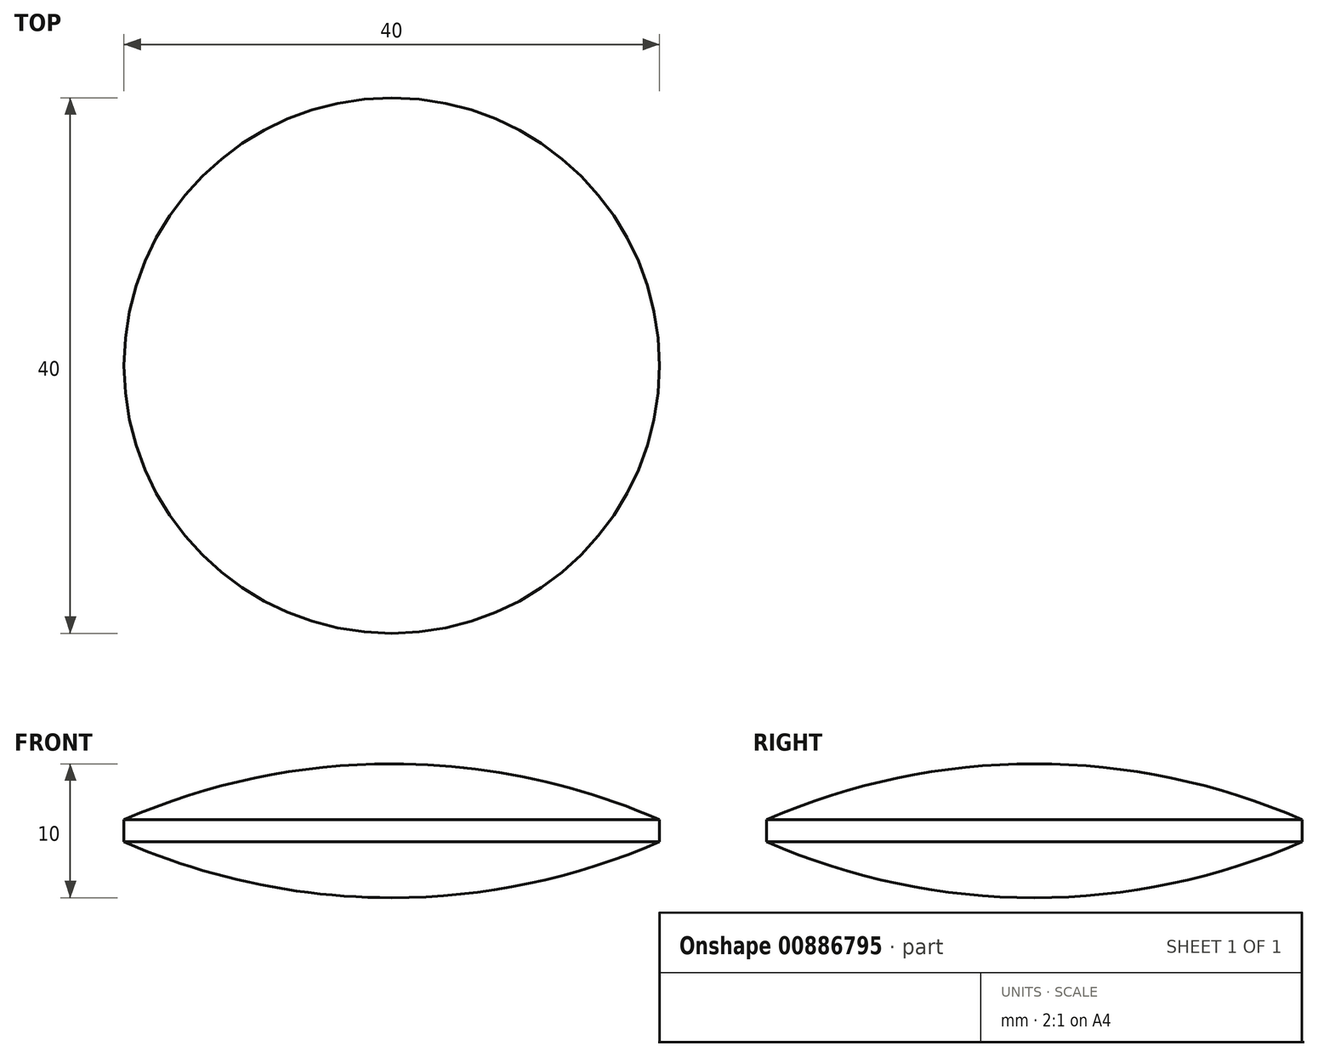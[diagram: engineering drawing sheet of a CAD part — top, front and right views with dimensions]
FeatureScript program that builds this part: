
annotation { "Feature Type Name" : "Feature", "Feature Type Description" : "" }
export const myFeature = defineFeature(function(context is Context, id is Id, definition is map)
    precondition{}
    {
        {
            var Q0;
            Q0=qCreatedBy(makeId("Front.planeOp"),FACE);
            var sketch = newSketch(context, id + "F0", { "sketchPlane" : qUnion([Q0])});
            skArc(sketch, "E0", {"start": v(-20, -0.83) * mm, "mid": v(-10.22, -3.95) * mm, "end": v(0, -5) * mm});
            skArc(sketch, "E1", {"start": v(0, 5) * mm, "mid": v(-10.22, 3.95) * mm, "end": v(-20, 0.83) * mm});
            skLineSegment(sketch, "E2", {"start": v(0, -5) * mm, "end": v(0, 5) * mm});
            skLineSegment(sketch, "E3", {"start": v(-20, -0.83) * mm, "end": v(-20, 0.83) * mm});
            skPoint(sketch, "E4.orphan", {"position": v(-20, -6.59) * mm});
            skSolve(sketch);
        }
        {
            var Q0;
            Q0=makeQuery(id+"F0.imprint","IMPRINT",FACE,{"disambiguationData":[TD([[makeQuery(id+"F0.imprint","IMPRINT",EDGE,{"derivedFrom":sQuery(id+"F0.wireOp",EDGE,"E0")}),1.0]])]});
            var Q1;
            Q1=sQuery(id+"F0.wireOp",EDGE,"E2");
            revolve(context, id + "F1", {"surfaceOperationType" : NewSurfaceOperationType.NEW, "entities" : qUnion([Q0]), "axis" : qUnion([Q1]), "revolveType" : RevolveType.FULL});
        }
    });
